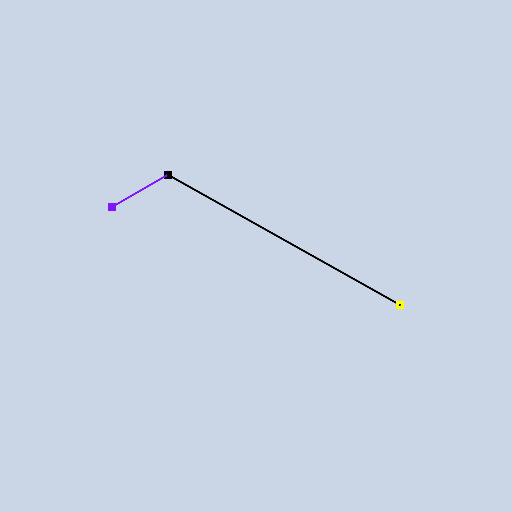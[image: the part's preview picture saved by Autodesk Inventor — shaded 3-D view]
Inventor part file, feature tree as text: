
AUTODESK INVENTOR PART (.ipt)
format: ipt  version: 2025 (Build 290162000, 162)  size: 88,576 bytes
history: native  units: in
note: dims shown in document units (in); Inventor stores cm internally (conversion verified against a paired STEP export)
features: other x2, plane x1, sketch x1
ambient origin geometry x8: Origin, YZ Plane, XZ Plane, XY Plane, X Axis, Y Axis, Z Axis, Center Point
feature tree (4):
  other  "Work Point1"
  other  "Work Point2"
  plane  "Work Plane1"
  sketch  "3D Sketch1"
